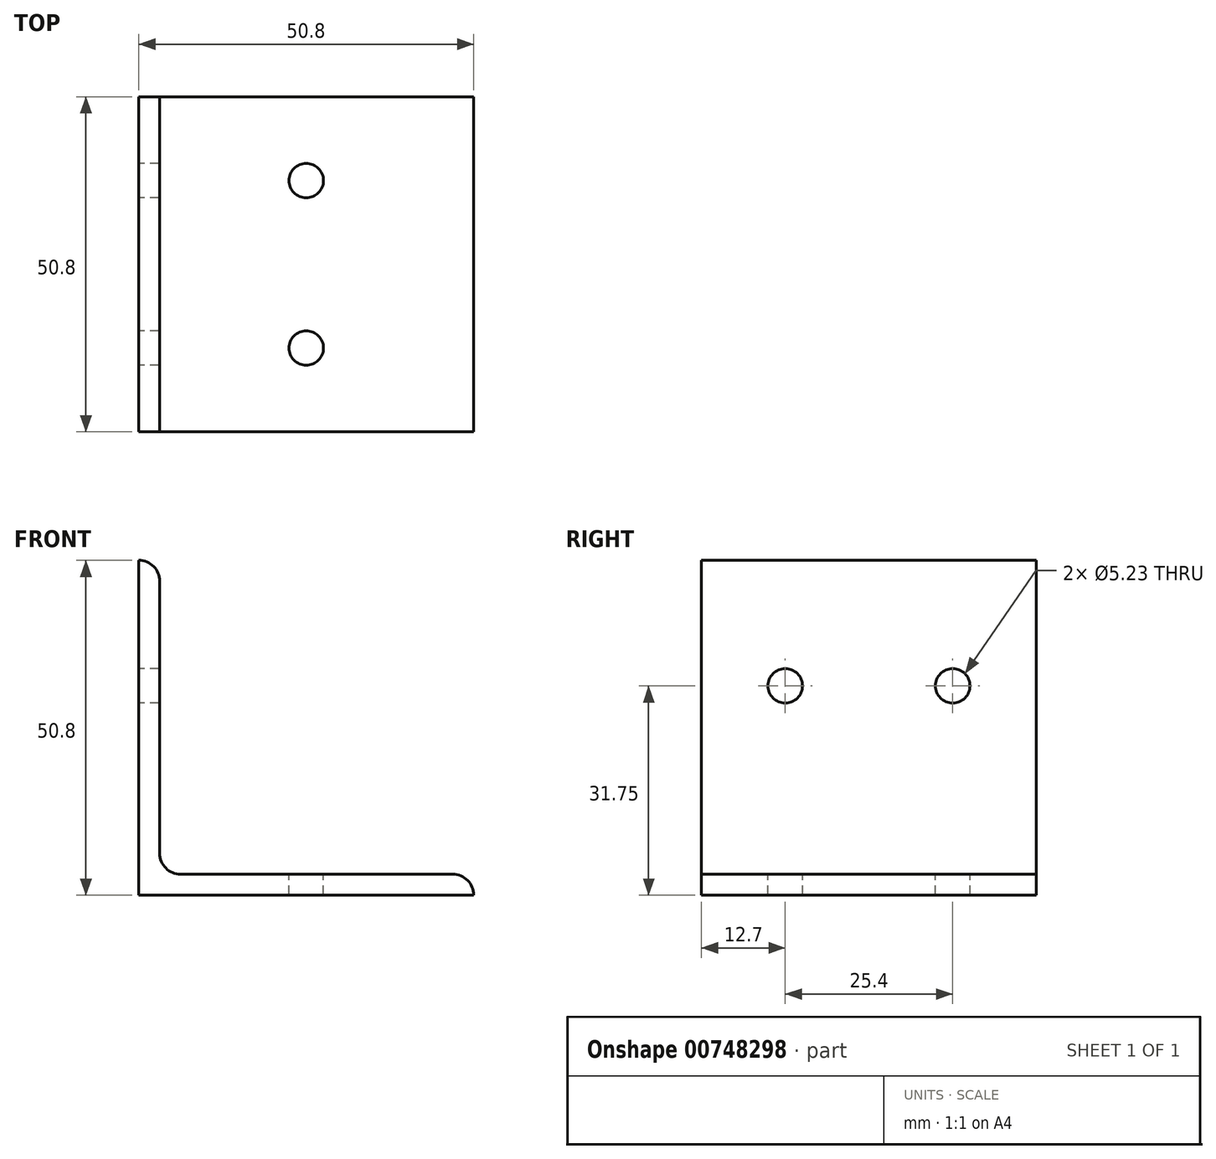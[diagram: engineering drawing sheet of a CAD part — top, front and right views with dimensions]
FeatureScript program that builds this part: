
annotation { "Feature Type Name" : "Feature", "Feature Type Description" : "" }
export const myFeature = defineFeature(function(context is Context, id is Id, definition is map)
    precondition{}
    {
        {
            var Q0;
            Q0=qCreatedBy(makeId("Front.planeOp"),FACE);
            var sketch = newSketch(context, id + "F0", { "sketchPlane" : qUnion([Q0])});
            skLineSegment(sketch, "E0", {"start": v(0, 0) * mm, "end": v(-50.8, 0) * mm});
            skLineSegment(sketch, "E1", {"start": v(-50.8, 0) * mm, "end": v(-50.8, 50.8) * mm});
            skLineSegment(sketch, "E2", {"start": v(-50.8, 50.8) * mm, "end": v(-50.8, 50.8) * mm});
            skLineSegment(sketch, "E3", {"start": v(-47.63, 47.63) * mm, "end": v(-47.63, 6.35) * mm});
            skLineSegment(sketch, "E4", {"start": v(-44.45, 3.18) * mm, "end": v(-3.18, 3.18) * mm});
            skLineSegment(sketch, "E5", {"start": v(0, 0) * mm, "end": v(0, 0) * mm});
            skPoint(sketch, "E6.visualSharp", {"position": v(-47.63, 3.18) * mm});
            skArc(sketch, "E6.filletArc", {"start": v(-47.63, 6.35) * mm, "mid": v(-46.7, 4.1) * mm, "end": v(-44.45, 3.18) * mm});
            skPoint(sketch, "E7.visualSharp", {"position": v(-47.63, 50.8) * mm});
            skArc(sketch, "E7.filletArc", {"start": v(-47.63, 47.63) * mm, "mid": v(-48.55, 49.87) * mm, "end": v(-50.8, 50.8) * mm});
            skPoint(sketch, "E8.visualSharp", {"position": v(0, 3.18) * mm});
            skArc(sketch, "E8.filletArc", {"start": v(0, 0) * mm, "mid": v(-0.93, 2.25) * mm, "end": v(-3.18, 3.18) * mm});
            skSolve(sketch);
        }
        {
            var Q0;
            Q0=qSketchRegion(id+"F0",true);
            extrude(context, id + "F1", {"entities" : qUnion([Q0]), "depth" : 50.8 * mm, "offsetDistance" : 25.4 * mm});
        }
        {
            var Q0;
            Q0=makeQuery(id+"F1.opExtrude","SWEPT_FACE",FACE,{"disambiguationData":[OSD([sQuery(id+"F0.wireOp",EDGE,"E4")])]});
            var sketch = newSketch(context, id + "F2", { "sketchPlane" : qUnion([Q0])});
            skLineSegment(sketch, "E9", {"start": v(-25.4, -50.8) * mm, "end": v(-25.4, 0) * mm, "construction": true});
            skLineSegment(sketch, "E10", {"start": v(-3.18, -38.1) * mm, "end": v(-44.45, -38.1) * mm, "construction": true});
            skCircle(sketch, "E11", {"center": v(-25.4, -38.1) * mm, "radius": 2.62 * mm});
            skLineSegment(sketch, "E12", {"start": v(-44.45, -12.7) * mm, "end": v(-3.18, -12.7) * mm, "construction": true});
            skCircle(sketch, "E13", {"center": v(-25.4, -12.7) * mm, "radius": 2.62 * mm});
            skLineSegment(sketch, "E14", {"start": v(-44.45, -25.4) * mm, "end": v(-3.18, -25.4) * mm, "construction": true});
            skSolve(sketch);
        }
        {
            var Q0;
            Q0=qSketchRegion(id+"F2",true);
            extrude(context, id + "F3", {"entities" : qUnion([Q0]), "operationType" : NewBodyOperationType.REMOVE, "endBound" : BoundingType.THROUGH_ALL, "oppositeDirection" : true, "depth" : 25.4 * mm, "offsetDistance" : 25.4 * mm});
        }
        {
            var Q0;
            Q0=makeQuery(id+"F1.opExtrude","SWEPT_FACE",FACE,{"disambiguationData":[OSD([sQuery(id+"F0.wireOp",EDGE,"E1")])]});
            var sketch = newSketch(context, id + "F4", { "sketchPlane" : qUnion([Q0])});
            skLineSegment(sketch, "E15", {"start": v(0, 31.75) * mm, "end": v(50.8, 31.75) * mm, "construction": true});
            skLineSegment(sketch, "E16", {"start": v(25.4, 50.8) * mm, "end": v(25.4, 0) * mm, "construction": true});
            skLineSegment(sketch, "E17", {"start": v(25.4, 0) * mm, "end": v(23.18, 0.53) * mm, "construction": true});
            skLineSegment(sketch, "E18", {"start": v(12.7, 50.8) * mm, "end": v(12.7, 0) * mm, "construction": true});
            skLineSegment(sketch, "E19", {"start": v(12.7, 0) * mm, "end": v(10.52, -0.15) * mm, "construction": true});
            skLineSegment(sketch, "E20", {"start": v(38.1, 50.8) * mm, "end": v(38.1, 0) * mm, "construction": true});
            skCircle(sketch, "E21", {"center": v(12.7, 31.75) * mm, "radius": 2.62 * mm});
            skCircle(sketch, "E22", {"center": v(38.1, 31.75) * mm, "radius": 2.62 * mm});
            skSolve(sketch);
        }
        {
            var Q0;
            Q0=qSketchRegion(id+"F4",true);
            extrude(context, id + "F5", {"entities" : qUnion([Q0]), "operationType" : NewBodyOperationType.REMOVE, "endBound" : BoundingType.THROUGH_ALL, "oppositeDirection" : true, "depth" : 25.4 * mm, "offsetDistance" : 25.4 * mm});
        }
    });
